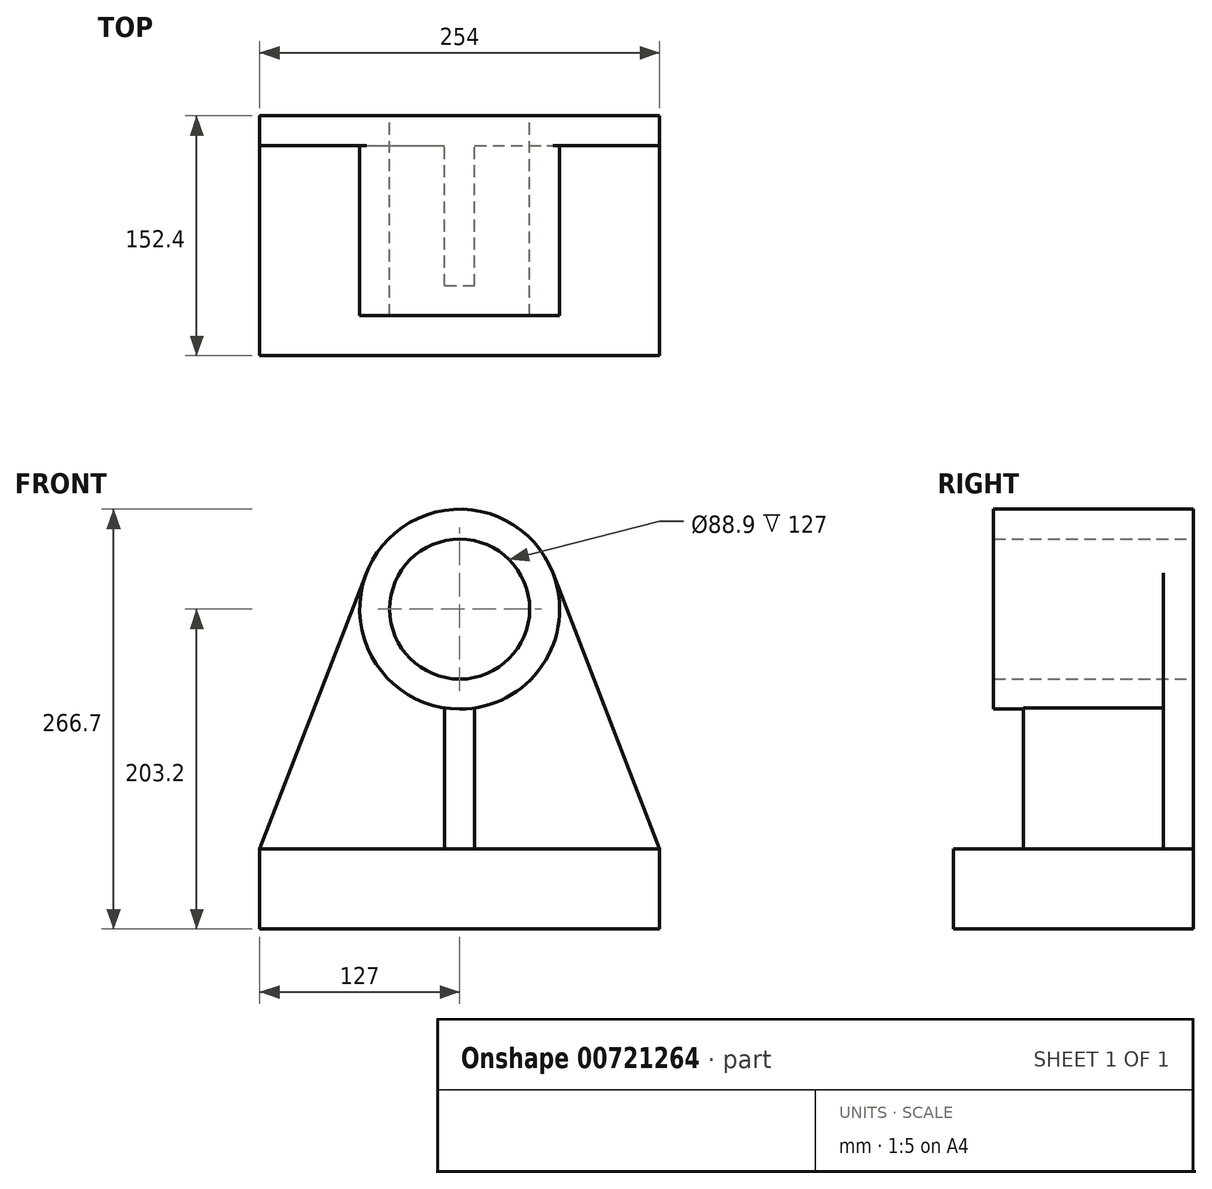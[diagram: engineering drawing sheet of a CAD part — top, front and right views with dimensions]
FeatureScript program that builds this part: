
annotation { "Feature Type Name" : "Feature", "Feature Type Description" : "" }
export const myFeature = defineFeature(function(context is Context, id is Id, definition is map)
    precondition{}
    {
        {
            var Q0;
            Q0=qCreatedBy(makeId("Front.planeOp"),FACE);
            var sketch = newSketch(context, id + "F0", { "sketchPlane" : qUnion([Q0])});
            skCircle(sketch, "E0", {"center": v(0, 0) * mm, "radius": 63.5 * mm});
            skCircle(sketch, "E1", {"center": v(0, 0) * mm, "radius": 44.45 * mm});
            skLineSegment(sketch, "E2", {"start": v(-127, -152.4) * mm, "end": v(127, -152.4) * mm});
            skLineSegment(sketch, "E3", {"start": v(127, -152.4) * mm, "end": v(127, -203.2) * mm});
            skLineSegment(sketch, "E4", {"start": v(127, -203.2) * mm, "end": v(-127, -203.2) * mm});
            skLineSegment(sketch, "E5", {"start": v(-127, -203.2) * mm, "end": v(-127, -152.4) * mm});
            skLineSegment(sketch, "E6", {"start": v(-127, -152.4) * mm, "end": v(-59.23, 22.9) * mm});
            skLineSegment(sketch, "E7", {"start": v(127, -152.4) * mm, "end": v(59.23, 22.9) * mm});
            skLineSegment(sketch, "E8", {"start": v(-9.53, -62.78) * mm, "end": v(-9.53, -152.4) * mm});
            skPoint(sketch, "E8.endSnap0", {"position": v(0, -152.4) * mm});
            skLineSegment(sketch, "E9", {"start": v(9.53, -62.78) * mm, "end": v(9.53, -152.4) * mm});
            skSolve(sketch);
        }
        {
            var Q0;
            {var subQ0=sQuery(id+"F0.wireOp",EDGE,"E3");Q0=makeQuery(id+"F0.imprint","IMPRINT",FACE,{"disambiguationData":[TD([[makeQuery(id+"F0.imprint","IMPRINT",EDGE,{"derivedFrom":subQ0}),-1.0]])]});}
            extrude(context, id + "F1", {"entities" : qUnion([Q0]), "depth" : 152.4 * mm, "offsetDistance" : 25.4 * mm});
        }
        {
            var Q0;
            {var subQ0=sQuery(id+"F0.wireOp",EDGE,"E7");Q0=makeQuery(id+"F0.imprint","IMPRINT",FACE,{"disambiguationData":[TD([[makeQuery(id+"F0.imprint","IMPRINT",EDGE,{"derivedFrom":subQ0}),1.0]])]});}
            var Q1;
            {var subQ0=sQuery(id+"F0.wireOp",EDGE,"E6");Q1=makeQuery(id+"F0.imprint","IMPRINT",FACE,{"disambiguationData":[TD([[makeQuery(id+"F0.imprint","IMPRINT",EDGE,{"derivedFrom":subQ0}),-1.0]])]});}
            extrude(context, id + "F2", {"entities" : qUnion([Q0, Q1]), "operationType" : NewBodyOperationType.ADD, "depth" : 19.05 * mm, "offsetDistance" : 25.4 * mm});
        }
        {
            var Q0;
            Q0=makeQuery(id+"F0.imprint","IMPRINT",FACE,{"disambiguationData":[TD([[makeQuery(id+"F0.imprint","IMPRINT",EDGE,{"derivedFrom":sQuery(id+"F0.wireOp",EDGE,"E1")}),-1.0]])]});
            extrude(context, id + "F3", {"entities" : qUnion([Q0]), "operationType" : NewBodyOperationType.ADD, "depth" : 127 * mm, "offsetDistance" : 25.4 * mm});
        }
        {
            var Q0;
            {var subQ0=sQuery(id+"F0.wireOp",EDGE,"E8");Q0=makeQuery(id+"F0.imprint","IMPRINT",FACE,{"disambiguationData":[TD([[makeQuery(id+"F0.imprint","IMPRINT",EDGE,{"derivedFrom":subQ0}),1.0]])]});}
            extrude(context, id + "F4", {"entities" : qUnion([Q0]), "operationType" : NewBodyOperationType.ADD, "depth" : 107.95 * mm, "offsetDistance" : 25.4 * mm});
        }
    });
